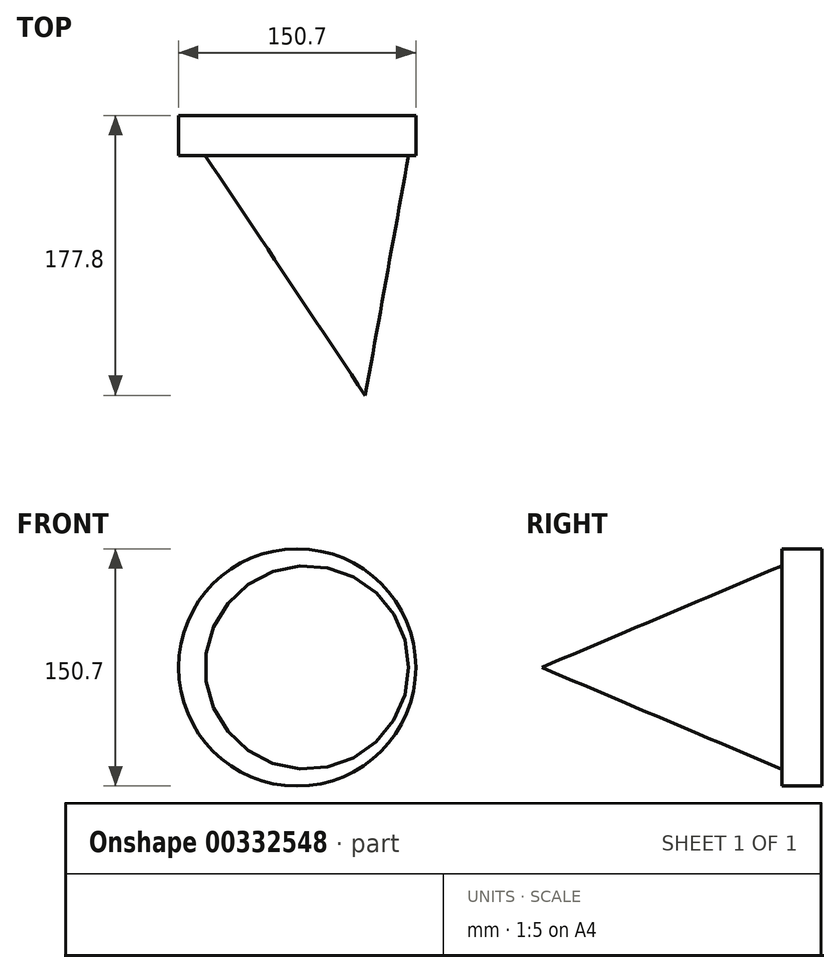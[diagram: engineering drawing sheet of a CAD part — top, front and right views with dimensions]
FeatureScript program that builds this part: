
annotation { "Feature Type Name" : "Feature", "Feature Type Description" : "" }
export const myFeature = defineFeature(function(context is Context, id is Id, definition is map)
    precondition{}
    {
        {
            var Q0;
            Q0=qCreatedBy(makeId("Front.planeOp"),FACE);
            var sketch = newSketch(context, id + "F0", { "sketchPlane" : qUnion([Q0])});
            skCircle(sketch, "E0", {"center": v(0, 0) * mm, "radius": 75.35 * mm});
            skSolve(sketch);
        }
        {
            var Q0;
            Q0=qCreatedBy(makeId("Front.planeOp"),FACE);
            cPlane(context, id + "F1", {"entities" : qUnion([Q0]), "cplaneType" : CPlaneType.OFFSET, "offset" : 177.8 * mm, "width" : 152.4 * mm, "height" : 152.4 * mm});
        }
        {
            var Q0;
            Q0=qCreatedBy(id+"F1.planeOp",FACE);
            var sketch = newSketch(context, id + "F2", { "sketchPlane" : qUnion([Q0])});
            skPoint(sketch, "E1", {"position": v(43.23, 0) * mm});
            skSolve(sketch);
        }
        {
            var Q0;
            Q0=sQuery(id+"F2.wireOp",VERTEX,"E1");
            var Q1;
            Q1=makeQuery(id+"F0.imprint","IMPRINT",FACE,{"disambiguationData":[TD([[makeQuery(id+"F0.imprint","IMPRINT",EDGE,{"derivedFrom":sQuery(id+"F0.wireOp",EDGE,"E0")}),1.0]])]});
            loft(context, id + "F3", {"sheetProfilesArray" : [{ "sheetProfileEntities" : qUnion([Q0]) }, { "sheetProfileEntities" : qUnion([Q1]) }]});
        }
        {
            var Q0;
            Q0=makeQuery(id+"F3.opLoft","CAP_FACE",FACE,{"disambiguationData":[OSD([makeQuery(id+"F0.imprint","IMPRINT",FACE,{"disambiguationData":[TD([[makeQuery(id+"F0.imprint","IMPRINT",EDGE,{"derivedFrom":sQuery(id+"F0.wireOp",EDGE,"E0")}),1.0]])]})])],"isStart":true});
            extrude(context, id + "F4", {"entities" : qUnion([Q0]), "operationType" : NewBodyOperationType.ADD, "oppositeDirection" : true, "depth" : 25.4 * mm});
        }
    });
